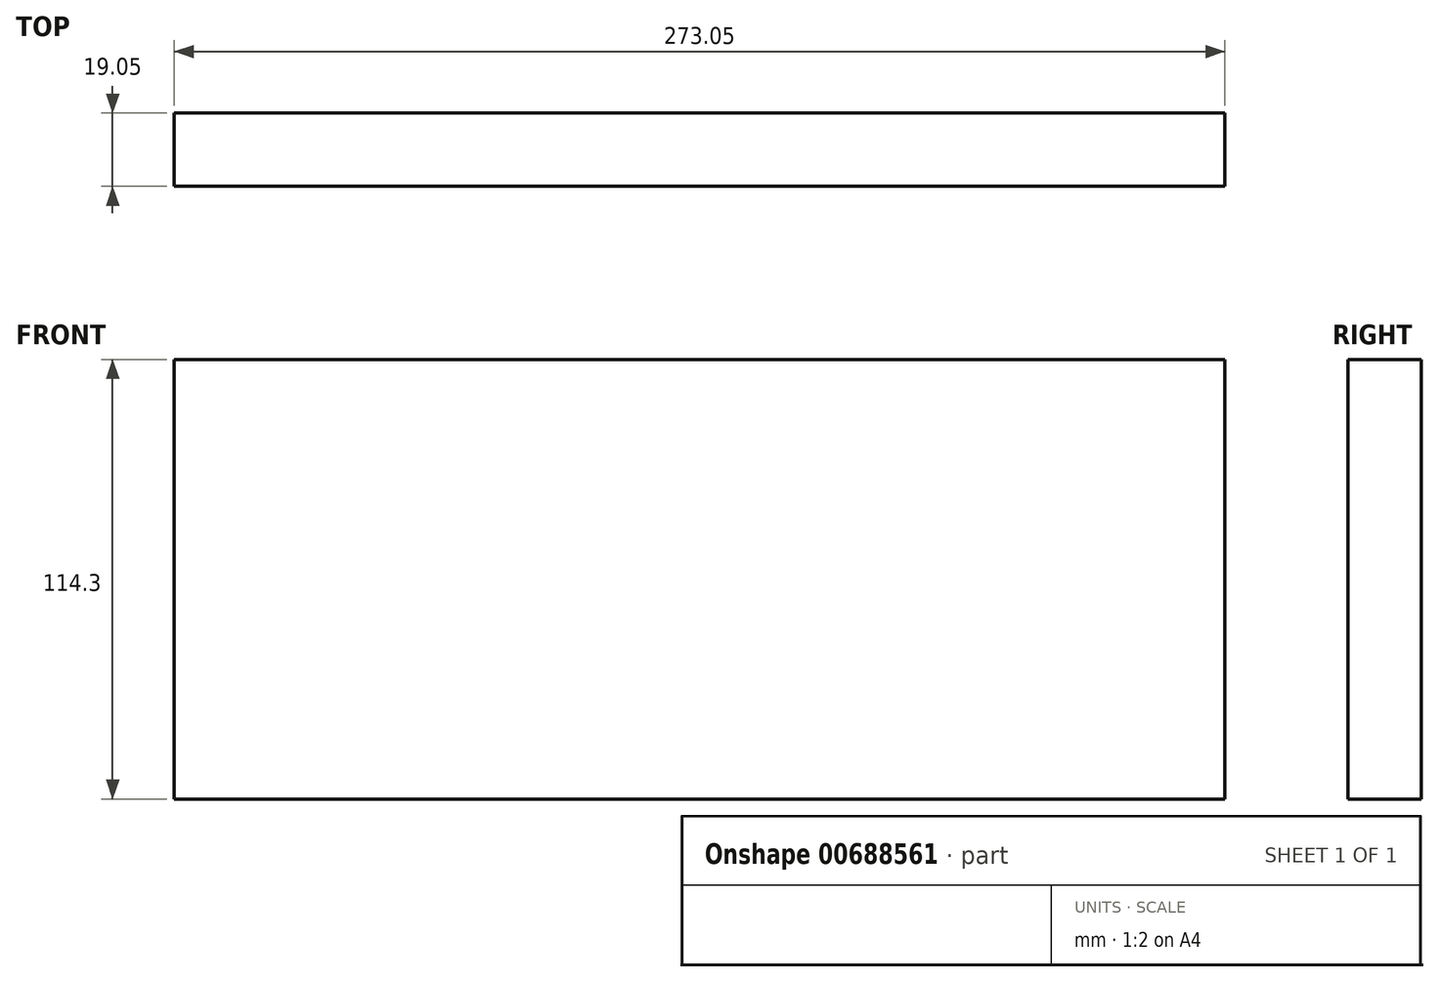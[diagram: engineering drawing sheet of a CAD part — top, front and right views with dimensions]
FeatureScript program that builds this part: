
annotation { "Feature Type Name" : "Feature", "Feature Type Description" : "" }
export const myFeature = defineFeature(function(context is Context, id is Id, definition is map)
    precondition{}
    {
        {
            var Q0;
            Q0=qCreatedBy(makeId("Front.planeOp"),FACE);
            var sketch = newSketch(context, id + "F0", { "sketchPlane" : qUnion([Q0])});
            skLineSegment(sketch, "E0.bottom", {"start": v(0, 0) * mm, "end": v(273.05, 0) * mm});
            skLineSegment(sketch, "E0.top", {"start": v(0, 114.3) * mm, "end": v(273.05, 114.3) * mm});
            skLineSegment(sketch, "E0.left", {"start": v(0, 0) * mm, "end": v(0, 114.3) * mm});
            skLineSegment(sketch, "E0.right", {"start": v(273.05, 0) * mm, "end": v(273.05, 114.3) * mm});
            skSolve(sketch);
        }
        {
            var Q0;
            Q0=qSketchRegion(id+"F0",true);
            extrude(context, id + "F1", {"entities" : qUnion([Q0]), "depth" : 19.05 * mm, "offsetDistance" : 25.4 * mm});
        }
    });
